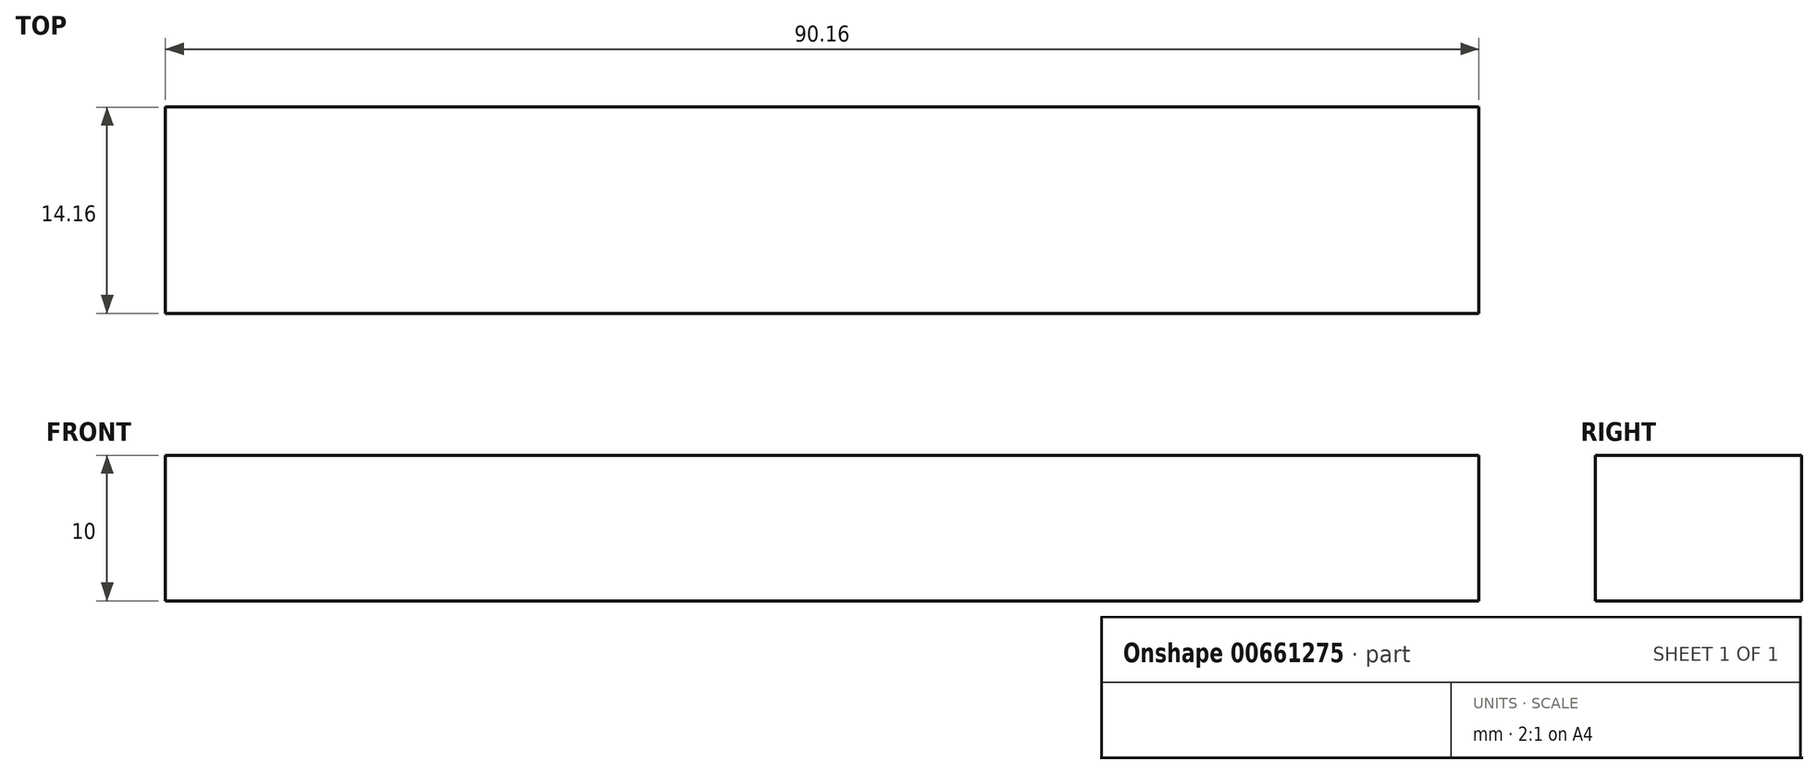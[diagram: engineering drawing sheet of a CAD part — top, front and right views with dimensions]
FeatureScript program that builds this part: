
annotation { "Feature Type Name" : "Feature", "Feature Type Description" : "" }
export const myFeature = defineFeature(function(context is Context, id is Id, definition is map)
    precondition{}
    {
        {
            var Q0;
            Q0=qCreatedBy(makeId("Top.planeOp"),FACE);
            var sketch = newSketch(context, id + "F0", { "sketchPlane" : qUnion([Q0])});
            skLineSegment(sketch, "E0.bottom", {"start": v(45.08, 7.08) * mm, "end": v(-45.08, 7.08) * mm});
            skLineSegment(sketch, "E0.top", {"start": v(45.08, -7.08) * mm, "end": v(-45.08, -7.08) * mm});
            skLineSegment(sketch, "E0.left", {"start": v(45.08, 7.08) * mm, "end": v(45.08, -7.08) * mm});
            skLineSegment(sketch, "E0.right", {"start": v(-45.08, 7.08) * mm, "end": v(-45.08, -7.08) * mm});
            skPoint(sketch, "E0.middle", {"position": v(0, 0) * mm});
            skSolve(sketch);
        }
        {
            var Q0;
            Q0=makeQuery(id+"F0.imprint","IMPRINT",FACE,{"disambiguationData":[TD([[makeQuery(id+"F0.imprint","IMPRINT",EDGE,{"derivedFrom":sQuery(id+"F0.wireOp",EDGE,"E0.bottom")}),1.0]])]});
            extrude(context, id + "F1", {"entities" : qUnion([Q0]), "depth" : 10 * mm, "offsetDistance" : 25 * mm});
        }
    });
